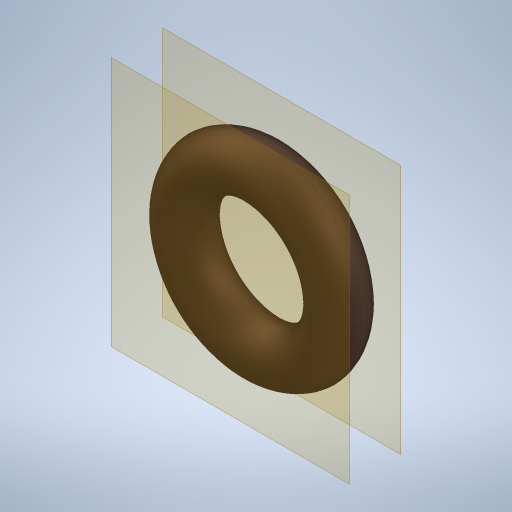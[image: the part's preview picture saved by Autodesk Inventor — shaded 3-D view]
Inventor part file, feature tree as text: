
AUTODESK INVENTOR PART (.ipt)
format: ipt  version: 2024 (Build 280153000, 153)  size: 326,656 bytes
history: native  units: in
note: dims shown in document units (in); Inventor stores cm internally (conversion verified against a paired STEP export)
features: other x3, plane x2
ambient origin geometry x8: Origin, YZ Plane, XZ Plane, XY Plane, X Axis, Y Axis, Z Axis, Center Point
bodies: Solid1 (feature_tree)
feature tree (5):
  other  "SA O-Ring.ipt"
  other  "Solid1::SA O-Ring.ipt"
  other  "TaggingFeature1"
  plane  "Work Plane1"
  plane  "Work Plane2"
